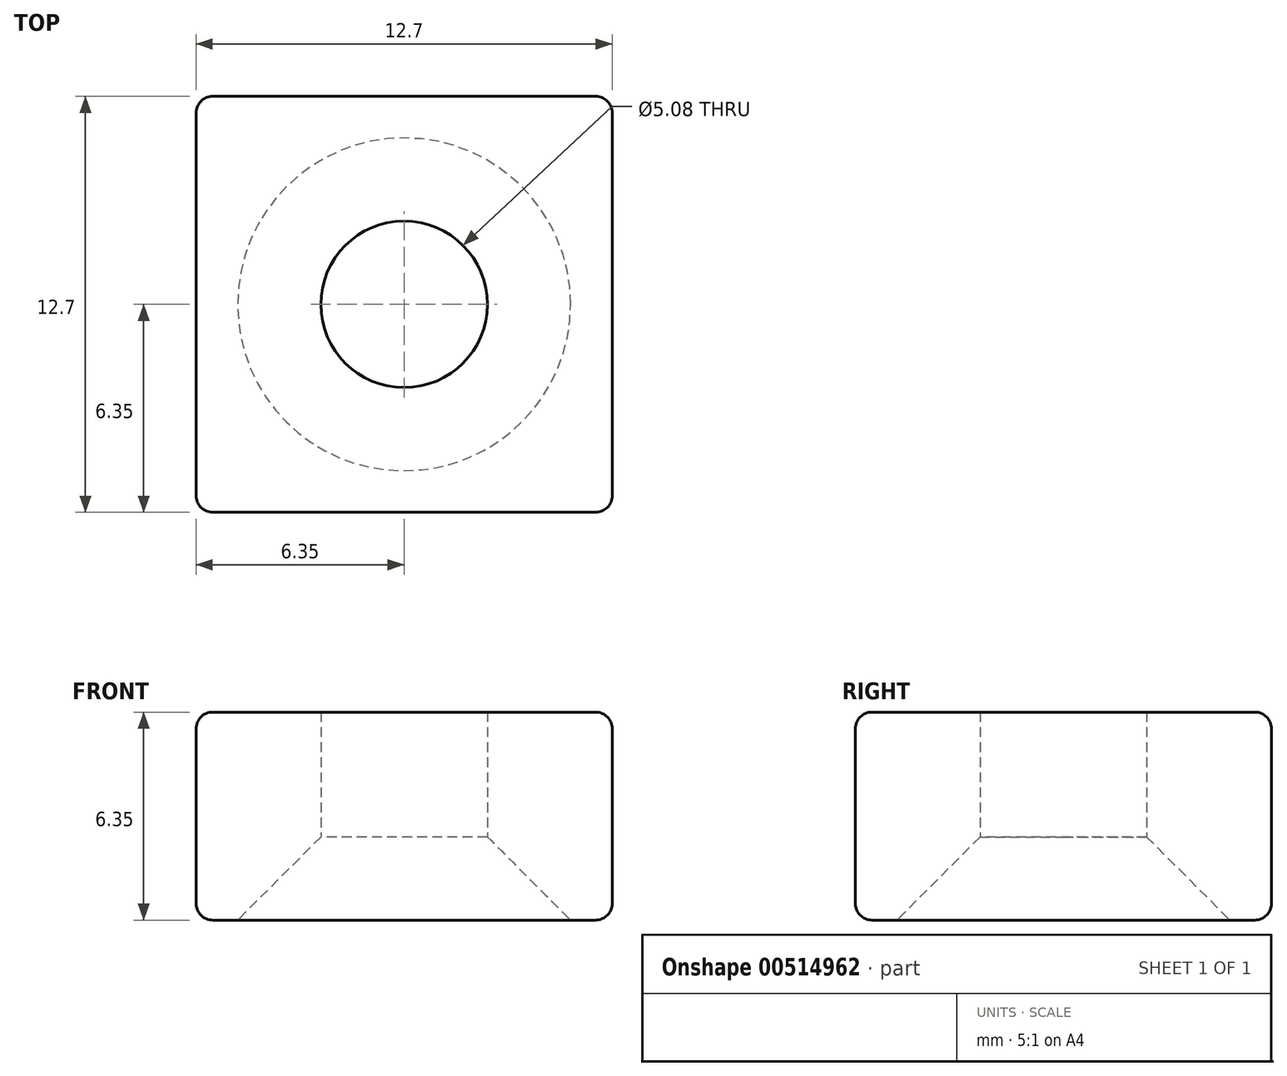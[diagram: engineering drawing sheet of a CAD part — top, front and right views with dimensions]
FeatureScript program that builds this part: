
annotation { "Feature Type Name" : "Feature", "Feature Type Description" : "" }
export const myFeature = defineFeature(function(context is Context, id is Id, definition is map)
    precondition{}
    {
        {
            var Q0;
            Q0=qCreatedBy(makeId("Top.planeOp"),FACE);
            var sketch = newSketch(context, id + "F0", { "sketchPlane" : qUnion([Q0])});
            skLineSegment(sketch, "E0.bottom", {"start": v(6.35, 6.35) * mm, "end": v(-6.35, 6.35) * mm});
            skLineSegment(sketch, "E0.top", {"start": v(6.35, -6.35) * mm, "end": v(-6.35, -6.35) * mm});
            skLineSegment(sketch, "E0.left", {"start": v(6.35, 6.35) * mm, "end": v(6.35, -6.35) * mm});
            skLineSegment(sketch, "E0.right", {"start": v(-6.35, 6.35) * mm, "end": v(-6.35, -6.35) * mm});
            skPoint(sketch, "E0.middle", {"position": v(0, 0) * mm});
            skCircle(sketch, "E1", {"center": v(0, 0) * mm, "radius": 2.54 * mm});
            skSolve(sketch);
        }
        {
            var Q0;
            Q0=makeQuery(id+"F0.imprint","IMPRINT",FACE,{"disambiguationData":[TD([[makeQuery(id+"F0.imprint","IMPRINT",EDGE,{"derivedFrom":sQuery(id+"F0.wireOp",EDGE,"E0.bottom")}),1.0]])]});
            extrude(context, id + "F1", {"entities" : qUnion([Q0]), "depth" : 6.35 * mm, "offsetDistance" : 25.4 * mm});
        }
        {
            var Q0;
            Q0=makeQuery(id+"F1.opExtrude","CAP_EDGE",EDGE,{"disambiguationData":[OSD([sQuery(id+"F0.wireOp",EDGE,"E1")])],"isStart":true});
            chamfer(context, id + "F2", {"entities" : qUnion([Q0]), "width" : 2.54 * mm, "tangentPropagation" : true});
        }
        {
            var Q0;
            Q0=makeQuery(id+"F1.opExtrude","CAP_EDGE",EDGE,{"disambiguationData":[OSD([sQuery(id+"F0.wireOp",EDGE,"E0.top")])],"isStart":true});
            var Q1;
            Q1=makeQuery(id+"F1.opExtrude","CAP_EDGE",EDGE,{"disambiguationData":[OSD([sQuery(id+"F0.wireOp",EDGE,"E0.left")])],"isStart":true});
            var Q2;
            Q2=makeQuery(id+"F1.opExtrude","CAP_EDGE",EDGE,{"disambiguationData":[OSD([sQuery(id+"F0.wireOp",EDGE,"E0.bottom")])],"isStart":true});
            var Q3;
            Q3=makeQuery(id+"F1.opExtrude","CAP_EDGE",EDGE,{"disambiguationData":[OSD([sQuery(id+"F0.wireOp",EDGE,"E0.right")])],"isStart":true});
            var Q4;
            Q4=makeQuery(id+"F1.opExtrude","SWEPT_EDGE",EDGE,{"disambiguationData":[OSD([sQuery(id+"F0.wireOp",EDGE,"E0.top"),sQuery(id+"F0.wireOp",EDGE,"E0.right")])]});
            var Q5;
            Q5=makeQuery(id+"F1.opExtrude","SWEPT_EDGE",EDGE,{"disambiguationData":[OSD([sQuery(id+"F0.wireOp",EDGE,"E0.top"),sQuery(id+"F0.wireOp",EDGE,"E0.left")])]});
            var Q6;
            Q6=makeQuery(id+"F1.opExtrude","SWEPT_EDGE",EDGE,{"disambiguationData":[OSD([sQuery(id+"F0.wireOp",EDGE,"E0.bottom"),sQuery(id+"F0.wireOp",EDGE,"E0.left")])]});
            var Q7;
            Q7=makeQuery(id+"F1.opExtrude","SWEPT_EDGE",EDGE,{"disambiguationData":[OSD([sQuery(id+"F0.wireOp",EDGE,"E0.bottom"),sQuery(id+"F0.wireOp",EDGE,"E0.right")])]});
            var Q8;
            Q8=makeQuery(id+"F1.opExtrude","CAP_EDGE",EDGE,{"disambiguationData":[OSD([sQuery(id+"F0.wireOp",EDGE,"E0.bottom")])],"isStart":false});
            var Q9;
            Q9=makeQuery(id+"F1.opExtrude","CAP_EDGE",EDGE,{"disambiguationData":[OSD([sQuery(id+"F0.wireOp",EDGE,"E0.right")])],"isStart":false});
            var Q10;
            Q10=makeQuery(id+"F1.opExtrude","CAP_EDGE",EDGE,{"disambiguationData":[OSD([sQuery(id+"F0.wireOp",EDGE,"E0.top")])],"isStart":false});
            var Q11;
            Q11=makeQuery(id+"F1.opExtrude","CAP_EDGE",EDGE,{"disambiguationData":[OSD([sQuery(id+"F0.wireOp",EDGE,"E0.left")])],"isStart":false});
            fillet(context, id + "F3", {"entities" : qUnion([Q0, Q1, Q2, Q3, Q4, Q5, Q6, Q7, Q8, Q9, Q10, Q11]), "radius" : 0.5 * mm, "tangentPropagation" : true, "allowEdgeOverflow" : false});
        }
    });
